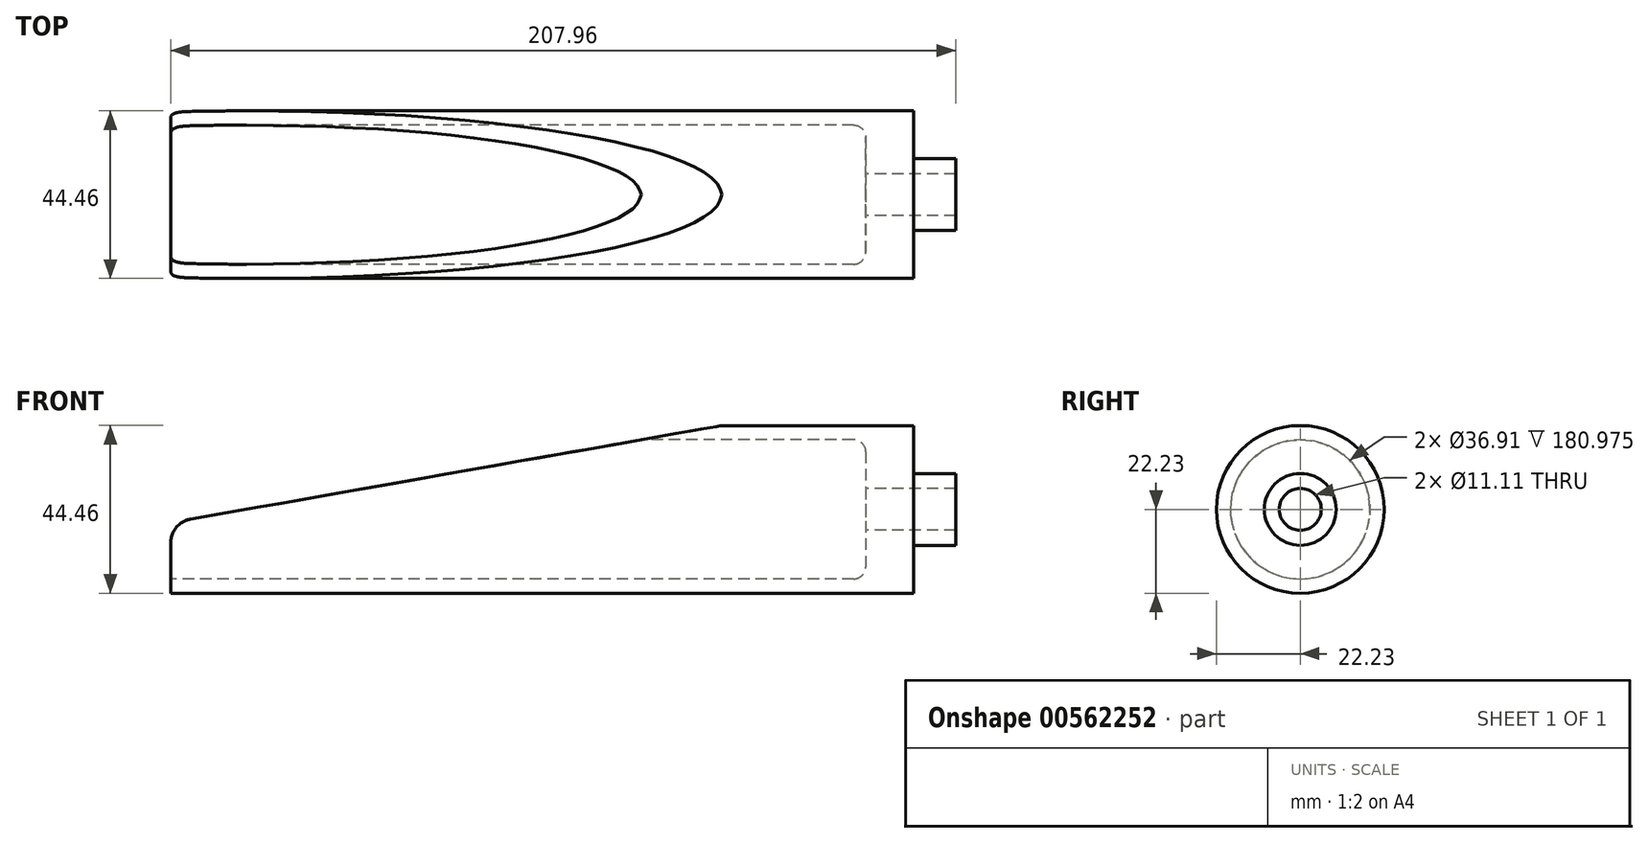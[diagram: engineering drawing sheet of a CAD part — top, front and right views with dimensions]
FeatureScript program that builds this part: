
annotation { "Feature Type Name" : "Feature", "Feature Type Description" : "" }
export const myFeature = defineFeature(function(context is Context, id is Id, definition is map)
    precondition{}
    {
        {
            var Q0;
            Q0=qCreatedBy(makeId("Front.planeOp"),FACE);
            var sketch = newSketch(context, id + "F0", { "sketchPlane" : qUnion([Q0])});
            skLineSegment(sketch, "E0", {"start": v(-207.96, 0) * mm, "end": v(0, 0) * mm, "construction": true});
            skLineSegment(sketch, "E1", {"start": v(0, 0) * mm, "end": v(0, 0) * mm});
            skLineSegment(sketch, "E2", {"start": v(0, -9.53) * mm, "end": v(-11.11, -9.53) * mm});
            skLineSegment(sketch, "E3", {"start": v(-11.11, -9.53) * mm, "end": v(-11.11, -22.23) * mm});
            skLineSegment(sketch, "E4", {"start": v(-11.11, -22.23) * mm, "end": v(-207.96, -22.23) * mm});
            skLineSegment(sketch, "E5", {"start": v(-207.96, -22.23) * mm, "end": v(-207.96, -18.46) * mm});
            skLineSegment(sketch, "E6", {"start": v(-207.96, -18.46) * mm, "end": v(-26.99, -18.46) * mm});
            skLineSegment(sketch, "E7", {"start": v(-23.81, -15.28) * mm, "end": v(-23.81, -5.56) * mm});
            skLineSegment(sketch, "E8", {"start": v(-23.81, 0) * mm, "end": v(0, 0) * mm, "construction": true});
            skLineSegment(sketch, "E9", {"start": v(0, 0) * mm, "end": v(0, -5.56) * mm, "construction": true});
            skPoint(sketch, "E10.visualSharp", {"position": v(-23.81, -18.46) * mm});
            skArc(sketch, "E10.filletArc", {"start": v(-26.99, -18.46) * mm, "mid": v(-24.74, -17.53) * mm, "end": v(-23.81, -15.28) * mm});
            skLineSegment(sketch, "E11", {"start": v(-23.81, -5.56) * mm, "end": v(0, -5.56) * mm});
            skLineSegment(sketch, "E12", {"start": v(-23.81, -5.56) * mm, "end": v(-23.81, 0) * mm, "construction": true});
            skLineSegment(sketch, "E13", {"start": v(0, -5.56) * mm, "end": v(0, -5.56) * mm});
            skLineSegment(sketch, "E14", {"start": v(0, -5.56) * mm, "end": v(0, -9.53) * mm});
            skSolve(sketch);
        }
        {
            var Q0;
            Q0 = qSketchRegion(id + "F0", true);
            var Q1;
            Q1=sQuery(id+"F0.wireOp",EDGE,"E0");
            revolve(context, id + "F1", {"entities" : qUnion([Q0]), "axis" : qUnion([Q1]), "revolveType" : RevolveType.FULL});
        }
        {
            var Q0;
            Q0=qCreatedBy(makeId("Front.planeOp"),FACE);
            var sketch = newSketch(context, id + "F2", { "sketchPlane" : qUnion([Q0])});
            skLineSegment(sketch, "E15", {"start": v(-214.31, 22.22) * mm, "end": v(-61.91, 22.22) * mm});
            skLineSegment(sketch, "E16", {"start": v(-61.91, 22.22) * mm, "end": v(-202.72, -2.6) * mm});
            skLineSegment(sketch, "E17", {"start": v(-207.96, -8.86) * mm, "end": v(-207.96, -22.23) * mm});
            skLineSegment(sketch, "E18", {"start": v(-207.96, -22.23) * mm, "end": v(-214.31, -22.23) * mm});
            skLineSegment(sketch, "E19", {"start": v(-214.31, -22.23) * mm, "end": v(-214.31, 22.23) * mm});
            skPoint(sketch, "E20.visualSharp", {"position": v(-207.96, -3.53) * mm});
            skArc(sketch, "E20.filletArc", {"start": v(-202.72, -2.6) * mm, "mid": v(-206.48, -4.77) * mm, "end": v(-207.96, -8.86) * mm});
            skLineSegment(sketch, "E21", {"start": v(-214.31, 0) * mm, "end": v(0, 0) * mm, "construction": true});
            skSolve(sketch);
        }
        {
            var Q0;
            Q0 = qSketchRegion(id + "F2", true);
            extrude(context, id + "F3", {"entities" : qUnion([Q0]), "operationType" : NewBodyOperationType.REMOVE, "oppositeDirection" : true, "depth" : 76.2 * mm, "offsetDistance" : 25.4 * mm, "symmetric" : true});
        }
    });
